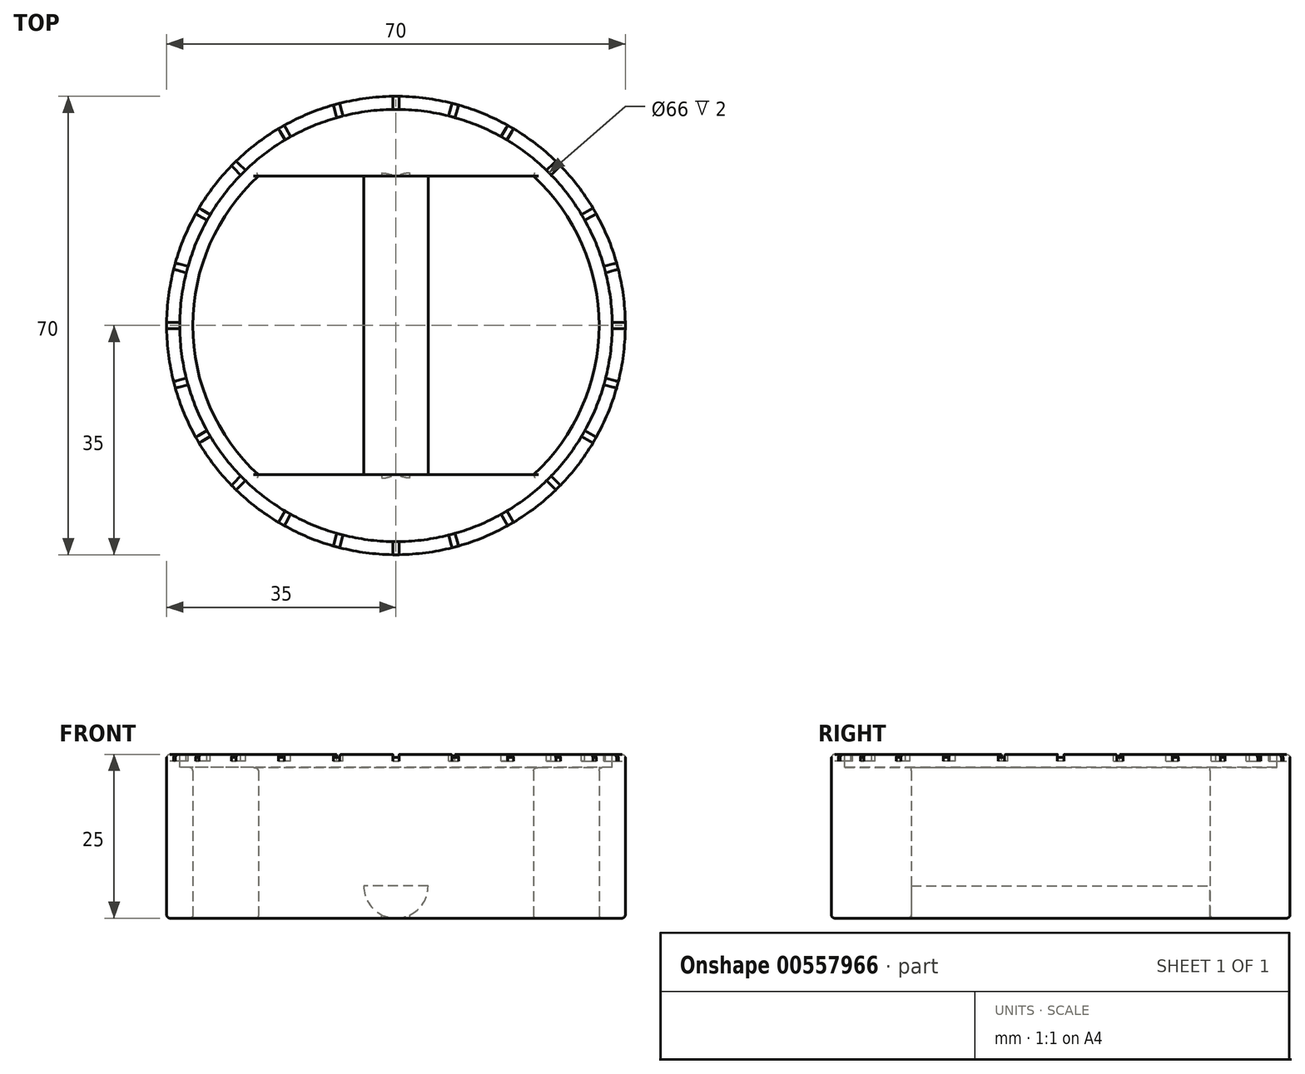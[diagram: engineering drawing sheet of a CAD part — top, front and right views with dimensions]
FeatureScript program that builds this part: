
annotation { "Feature Type Name" : "Feature", "Feature Type Description" : "" }
export const myFeature = defineFeature(function(context is Context, id is Id, definition is map)
    precondition{}
    {
        {
            var Q0;
            Q0=qCreatedBy(makeId("Top.planeOp"),FACE);
            var sketch = newSketch(context, id + "F0", { "sketchPlane" : qUnion([Q0])});
            skCircle(sketch, "E0", {"center": v(0, 0) * mm, "radius": 35 * mm});
            skLineSegment(sketch, "E1", {"start": v(-21, -22.8) * mm, "end": v(21, -22.8) * mm});
            skLineSegment(sketch, "E2", {"start": v(-21, 22.8) * mm, "end": v(21, 22.8) * mm});
            skArc(sketch, "E3", {"start": v(-21, 22.8) * mm, "mid": v(-31, 0) * mm, "end": v(-21, -22.8) * mm});
            skArc(sketch, "E4.trimOffspring", {"start": v(21, -22.8) * mm, "mid": v(31, 0) * mm, "end": v(21, 22.8) * mm});
            skSolve(sketch);
        }
        {
            var Q0;
            Q0 = qSketchRegion(id + "F0", true);
            extrude(context, id + "F1", {"entities" : qUnion([Q0]), "depth" : 25 * mm, "offsetDistance" : 25 * mm});
        }
        {
            var Q0;
            Q0=makeQuery(id+"F1.opExtrude","CAP_FACE",FACE,{"disambiguationData":[OSD([sQuery(id+"F0.wireOp",EDGE,"E0"),sQuery(id+"F0.wireOp",EDGE,"E1"),sQuery(id+"F0.wireOp",EDGE,"E2"),sQuery(id+"F0.wireOp",EDGE,"E3"),sQuery(id+"F0.wireOp",EDGE,"E4.trimOffspring")])],"isStart":false});
            var sketch = newSketch(context, id + "F2", { "sketchPlane" : qUnion([Q0])});
            skCircle(sketch, "E5.0", {"center": v(0, 0) * mm, "radius": 33 * mm});
            skSolve(sketch);
        }
        {
            var Q0;
            Q0 = qSketchRegion(id + "F2", true);
            extrude(context, id + "F3", {"entities" : qUnion([Q0]), "operationType" : NewBodyOperationType.REMOVE, "oppositeDirection" : true, "depth" : 2 * mm, "offsetDistance" : 25 * mm});
        }
        {
            var Q0;
            Q0=qCreatedBy(makeId("Front.planeOp"),FACE);
            var sketch = newSketch(context, id + "F4", { "sketchPlane" : qUnion([Q0])});
            skArc(sketch, "E6", {"start": v(-4.9, 4.9) * mm, "mid": v(0, 0) * mm, "end": v(4.9, 4.9) * mm});
            skLineSegment(sketch, "E7", {"start": v(-4.9, 4.9) * mm, "end": v(4.9, 4.9) * mm});
            skSolve(sketch);
        }
        {
            var Q0;
            Q0 = qSketchRegion(id + "F4", true);
            var Q1;
            Q1=makeQuery(id+"F1.opExtrude","SWEPT_FACE",FACE,{"disambiguationData":[OSD([sQuery(id+"F0.wireOp",EDGE,"E1")])]});
            var Q2;
            Q2=makeQuery(id+"F1.opExtrude","SWEPT_FACE",FACE,{"disambiguationData":[OSD([sQuery(id+"F0.wireOp",EDGE,"E2")])]});
            extrude(context, id + "F5", {"entities" : qUnion([Q0]), "operationType" : NewBodyOperationType.ADD, "endBound" : BoundingType.UP_TO_SURFACE, "depth" : 25 * mm, "endBoundEntityFace" : qUnion([Q1]), "offsetDistance" : 25 * mm, "hasSecondDirection" : true, "secondDirectionBound" : BoundingType.UP_TO_SURFACE, "secondDirectionOppositeDirection" : true, "secondDirectionDepth" : 25 * mm, "secondDirectionBoundEntityFace" : qUnion([Q2])});
        }
        {
            var Q0;
            Q0=makeQuery(id+"F3.boolean.opBoolean","COPY",EDGE,{"derivedFrom":makeQuery(id+"F3.opExtrude","CAP_EDGE",EDGE,{"disambiguationData":[OSD([sQuery(id+"F2.wireOp",EDGE,"E5.0")])],"isStart":true})});
            var Q1;
            Q1=makeQuery(id+"F1.opExtrude","CAP_EDGE",EDGE,{"disambiguationData":[OSD([sQuery(id+"F0.wireOp",EDGE,"E0")])],"isStart":false});
            var Q2;
            Q2=makeQuery(id+"F3.boolean.opBoolean","INTERSECT",EDGE,{"derivedFrom":[makeQuery(id+"F1.opExtrude","SWEPT_FACE",FACE,{"disambiguationData":[OSD([sQuery(id+"F0.wireOp",EDGE,"E3")])]}),makeQuery(id+"F3.opExtrude","CAP_FACE",FACE,{"disambiguationData":[OSD([sQuery(id+"F2.wireOp",EDGE,"E5.0")])],"isStart":false})]});
            var Q3;
            Q3=makeQuery(id+"F3.boolean.opBoolean","INTERSECT",EDGE,{"derivedFrom":[makeQuery(id+"F1.opExtrude","SWEPT_FACE",FACE,{"disambiguationData":[OSD([sQuery(id+"F0.wireOp",EDGE,"E4.trimOffspring")])]}),makeQuery(id+"F3.opExtrude","CAP_FACE",FACE,{"disambiguationData":[OSD([sQuery(id+"F2.wireOp",EDGE,"E5.0")])],"isStart":false})]});
            var Q4;
            Q4=makeQuery(id+"F5.opExtrude","TWEAK_EDGE",EDGE,{"disambiguationData":[OD(0.0)],"derivedFrom":[makeQuery(id+"F4.imprint","IMPRINT",EDGE,{"derivedFrom":sQuery(id+"F4.wireOp",EDGE,"E6")}),makeQuery(id+"F4.imprint","IMPRINT",EDGE,{"derivedFrom":sQuery(id+"F4.wireOp",EDGE,"E7")})]});
            var Q5;
            Q5=makeQuery(id+"F5.opExtrude","TWEAK_EDGE",EDGE,{"disambiguationData":[OD(1.0)],"derivedFrom":[makeQuery(id+"F4.imprint","IMPRINT",EDGE,{"derivedFrom":sQuery(id+"F4.wireOp",EDGE,"E6")}),makeQuery(id+"F4.imprint","IMPRINT",EDGE,{"derivedFrom":sQuery(id+"F4.wireOp",EDGE,"E7")})]});
            var Q6;
            {var subQ0=sQuery(id+"F0.wireOp",EDGE,"E4.trimOffspring");var subQ1=sQuery(id+"F0.wireOp",EDGE,"E2");Q6=makeQuery(id+"F5.boolean.opBoolean","SPLIT",EDGE,{"disambiguationData":[TD([makeQuery(id+"F1.opExtrude","SWEPT_FACE",FACE,{"disambiguationData":[OSD([subQ0])]})])],"derivedFrom":makeQuery(id+"F1.opExtrude","CAP_EDGE",EDGE,{"disambiguationData":[OSD([subQ1])],"isStart":true})});}
            var Q7;
            {var subQ0=sQuery(id+"F0.wireOp",EDGE,"E3");var subQ1=sQuery(id+"F0.wireOp",EDGE,"E1");Q7=makeQuery(id+"F5.boolean.opBoolean","SPLIT",EDGE,{"disambiguationData":[TD([makeQuery(id+"F1.opExtrude","SWEPT_FACE",FACE,{"disambiguationData":[OSD([subQ0])]})])],"derivedFrom":makeQuery(id+"F1.opExtrude","CAP_EDGE",EDGE,{"disambiguationData":[OSD([subQ1])],"isStart":true})});}
            var Q8;
            Q8=makeQuery(id+"F1.opExtrude","CAP_EDGE",EDGE,{"disambiguationData":[OSD([sQuery(id+"F0.wireOp",EDGE,"E0")])],"isStart":true});
            var Q9;
            Q9=makeQuery(id+"F1.opExtrude","CAP_EDGE",EDGE,{"disambiguationData":[OSD([sQuery(id+"F0.wireOp",EDGE,"E3")])],"isStart":true});
            var Q10;
            Q10=makeQuery(id+"F1.opExtrude","CAP_EDGE",EDGE,{"disambiguationData":[OSD([sQuery(id+"F0.wireOp",EDGE,"E4.trimOffspring")])],"isStart":true});
            fillet(context, id + "F6", {"entities" : qUnion([Q0, Q1, Q2, Q3, Q4, Q5, Q6, Q7, Q8, Q9, Q10]), "radius" : 0.5 * mm, "tangentPropagation" : true, "allowEdgeOverflow" : false});
        }
        {
            var Q0;
            Q0=makeQuery(id+"F1.opExtrude","CAP_FACE",FACE,{"disambiguationData":[OSD([sQuery(id+"F0.wireOp",EDGE,"E0"),sQuery(id+"F0.wireOp",EDGE,"E1"),sQuery(id+"F0.wireOp",EDGE,"E2"),sQuery(id+"F0.wireOp",EDGE,"E3"),sQuery(id+"F0.wireOp",EDGE,"E4.trimOffspring")])],"isStart":false});
            var sketch = newSketch(context, id + "F7", { "sketchPlane" : qUnion([Q0])});
            skLineSegment(sketch, "E8.bottom", {"start": v(0.5, 33) * mm, "end": v(-0.5, 33) * mm});
            skLineSegment(sketch, "E8.top", {"start": v(0.5, 35) * mm, "end": v(-0.5, 35) * mm});
            skLineSegment(sketch, "E8.left", {"start": v(0.5, 33) * mm, "end": v(0.5, 35) * mm});
            skLineSegment(sketch, "E8.right", {"start": v(-0.5, 33) * mm, "end": v(-0.5, 35) * mm});
            skPoint(sketch, "E8.middle", {"position": v(0, 34) * mm});
            skLineSegment(sketch, "E9.1.0", {"start": v(9.54, 33.67) * mm, "end": v(8.57, 33.93) * mm});
            skLineSegment(sketch, "E9.1.1", {"start": v(9.02, 31.74) * mm, "end": v(8.06, 32) * mm});
            skPoint(sketch, "E9.1.2", {"position": v(8.8, 32.84) * mm});
            skLineSegment(sketch, "E9.1.3", {"start": v(8.06, 32) * mm, "end": v(8.57, 33.93) * mm});
            skLineSegment(sketch, "E9.1.4", {"start": v(9.02, 31.74) * mm, "end": v(9.54, 33.67) * mm});
            skLineSegment(sketch, "E9.2.0", {"start": v(17.93, 30.06) * mm, "end": v(17.07, 30.56) * mm});
            skLineSegment(sketch, "E9.2.1", {"start": v(16.93, 28.33) * mm, "end": v(16.07, 28.83) * mm});
            skPoint(sketch, "E9.2.2", {"position": v(17, 29.44) * mm});
            skLineSegment(sketch, "E9.2.3", {"start": v(16.07, 28.83) * mm, "end": v(17.07, 30.56) * mm});
            skLineSegment(sketch, "E9.2.4", {"start": v(16.93, 28.33) * mm, "end": v(17.93, 30.06) * mm});
            skLineSegment(sketch, "E9.3.0", {"start": v(25.1, 24.4) * mm, "end": v(24.4, 25.1) * mm});
            skLineSegment(sketch, "E9.3.1", {"start": v(23.69, 22.98) * mm, "end": v(22.98, 23.69) * mm});
            skPoint(sketch, "E9.3.2", {"position": v(24.04, 24.04) * mm});
            skLineSegment(sketch, "E9.3.3", {"start": v(22.98, 23.69) * mm, "end": v(24.4, 25.1) * mm});
            skLineSegment(sketch, "E9.3.4", {"start": v(23.69, 22.98) * mm, "end": v(25.1, 24.4) * mm});
            skLineSegment(sketch, "E9.4.0", {"start": v(30.56, 17.07) * mm, "end": v(30.06, 17.93) * mm});
            skLineSegment(sketch, "E9.4.1", {"start": v(28.83, 16.07) * mm, "end": v(28.33, 16.93) * mm});
            skPoint(sketch, "E9.4.2", {"position": v(29.44, 17) * mm});
            skLineSegment(sketch, "E9.4.3", {"start": v(28.33, 16.93) * mm, "end": v(30.06, 17.93) * mm});
            skLineSegment(sketch, "E9.4.4", {"start": v(28.83, 16.07) * mm, "end": v(30.56, 17.07) * mm});
            skLineSegment(sketch, "E9.5.0", {"start": v(33.93, 8.57) * mm, "end": v(33.67, 9.54) * mm});
            skLineSegment(sketch, "E9.5.1", {"start": v(32, 8.06) * mm, "end": v(31.74, 9.02) * mm});
            skPoint(sketch, "E9.5.2", {"position": v(32.84, 8.8) * mm});
            skLineSegment(sketch, "E9.5.3", {"start": v(31.74, 9.02) * mm, "end": v(33.67, 9.54) * mm});
            skLineSegment(sketch, "E9.5.4", {"start": v(32, 8.06) * mm, "end": v(33.93, 8.57) * mm});
            skLineSegment(sketch, "E9.6.0", {"start": v(35, -0.5) * mm, "end": v(35, 0.5) * mm});
            skLineSegment(sketch, "E9.6.1", {"start": v(33, -0.5) * mm, "end": v(33, 0.5) * mm});
            skPoint(sketch, "E9.6.2", {"position": v(34, 0) * mm});
            skLineSegment(sketch, "E9.6.3", {"start": v(33, 0.5) * mm, "end": v(35, 0.5) * mm});
            skLineSegment(sketch, "E9.6.4", {"start": v(33, -0.5) * mm, "end": v(35, -0.5) * mm});
            skLineSegment(sketch, "E9.7.0", {"start": v(33.67, -9.54) * mm, "end": v(33.93, -8.57) * mm});
            skLineSegment(sketch, "E9.7.1", {"start": v(31.74, -9.02) * mm, "end": v(32, -8.06) * mm});
            skPoint(sketch, "E9.7.2", {"position": v(32.84, -8.8) * mm});
            skLineSegment(sketch, "E9.7.3", {"start": v(32, -8.06) * mm, "end": v(33.93, -8.57) * mm});
            skLineSegment(sketch, "E9.7.4", {"start": v(31.74, -9.02) * mm, "end": v(33.67, -9.54) * mm});
            skLineSegment(sketch, "E9.8.0", {"start": v(30.06, -17.93) * mm, "end": v(30.56, -17.07) * mm});
            skLineSegment(sketch, "E9.8.1", {"start": v(28.33, -16.93) * mm, "end": v(28.83, -16.07) * mm});
            skPoint(sketch, "E9.8.2", {"position": v(29.44, -17) * mm});
            skLineSegment(sketch, "E9.8.3", {"start": v(28.83, -16.07) * mm, "end": v(30.56, -17.07) * mm});
            skLineSegment(sketch, "E9.8.4", {"start": v(28.33, -16.93) * mm, "end": v(30.06, -17.93) * mm});
            skLineSegment(sketch, "E9.9.0", {"start": v(24.4, -25.1) * mm, "end": v(25.1, -24.4) * mm});
            skLineSegment(sketch, "E9.9.1", {"start": v(22.98, -23.69) * mm, "end": v(23.69, -22.98) * mm});
            skPoint(sketch, "E9.9.2", {"position": v(24.04, -24.04) * mm});
            skLineSegment(sketch, "E9.9.3", {"start": v(23.69, -22.98) * mm, "end": v(25.1, -24.4) * mm});
            skLineSegment(sketch, "E9.9.4", {"start": v(22.98, -23.69) * mm, "end": v(24.4, -25.1) * mm});
            skLineSegment(sketch, "E9.10.0", {"start": v(17.07, -30.56) * mm, "end": v(17.93, -30.06) * mm});
            skLineSegment(sketch, "E9.10.1", {"start": v(16.07, -28.83) * mm, "end": v(16.93, -28.33) * mm});
            skPoint(sketch, "E9.10.2", {"position": v(17, -29.44) * mm});
            skLineSegment(sketch, "E9.10.3", {"start": v(16.93, -28.33) * mm, "end": v(17.93, -30.06) * mm});
            skLineSegment(sketch, "E9.10.4", {"start": v(16.07, -28.83) * mm, "end": v(17.07, -30.56) * mm});
            skLineSegment(sketch, "E9.11.0", {"start": v(8.57, -33.93) * mm, "end": v(9.54, -33.67) * mm});
            skLineSegment(sketch, "E9.11.1", {"start": v(8.06, -32) * mm, "end": v(9.02, -31.74) * mm});
            skPoint(sketch, "E9.11.2", {"position": v(8.8, -32.84) * mm});
            skLineSegment(sketch, "E9.11.3", {"start": v(9.02, -31.74) * mm, "end": v(9.54, -33.67) * mm});
            skLineSegment(sketch, "E9.11.4", {"start": v(8.06, -32) * mm, "end": v(8.57, -33.93) * mm});
            skLineSegment(sketch, "E9.12.0", {"start": v(-0.5, -35) * mm, "end": v(0.5, -35) * mm});
            skLineSegment(sketch, "E9.12.1", {"start": v(-0.5, -33) * mm, "end": v(0.5, -33) * mm});
            skPoint(sketch, "E9.12.2", {"position": v(0, -34) * mm});
            skLineSegment(sketch, "E9.12.3", {"start": v(0.5, -33) * mm, "end": v(0.5, -35) * mm});
            skLineSegment(sketch, "E9.12.4", {"start": v(-0.5, -33) * mm, "end": v(-0.5, -35) * mm});
            skLineSegment(sketch, "E9.13.0", {"start": v(-9.54, -33.67) * mm, "end": v(-8.57, -33.93) * mm});
            skLineSegment(sketch, "E9.13.1", {"start": v(-9.02, -31.74) * mm, "end": v(-8.06, -32) * mm});
            skPoint(sketch, "E9.13.2", {"position": v(-8.8, -32.84) * mm});
            skLineSegment(sketch, "E9.13.3", {"start": v(-8.06, -32) * mm, "end": v(-8.57, -33.93) * mm});
            skLineSegment(sketch, "E9.13.4", {"start": v(-9.02, -31.74) * mm, "end": v(-9.54, -33.67) * mm});
            skLineSegment(sketch, "E9.14.0", {"start": v(-17.93, -30.06) * mm, "end": v(-17.07, -30.56) * mm});
            skLineSegment(sketch, "E9.14.1", {"start": v(-16.93, -28.33) * mm, "end": v(-16.07, -28.83) * mm});
            skPoint(sketch, "E9.14.2", {"position": v(-17, -29.44) * mm});
            skLineSegment(sketch, "E9.14.3", {"start": v(-16.07, -28.83) * mm, "end": v(-17.07, -30.56) * mm});
            skLineSegment(sketch, "E9.14.4", {"start": v(-16.93, -28.33) * mm, "end": v(-17.93, -30.06) * mm});
            skLineSegment(sketch, "E9.15.0", {"start": v(-25.1, -24.4) * mm, "end": v(-24.4, -25.1) * mm});
            skLineSegment(sketch, "E9.15.1", {"start": v(-23.69, -22.98) * mm, "end": v(-22.98, -23.69) * mm});
            skPoint(sketch, "E9.15.2", {"position": v(-24.04, -24.04) * mm});
            skLineSegment(sketch, "E9.15.3", {"start": v(-22.98, -23.69) * mm, "end": v(-24.4, -25.1) * mm});
            skLineSegment(sketch, "E9.15.4", {"start": v(-23.69, -22.98) * mm, "end": v(-25.1, -24.4) * mm});
            skLineSegment(sketch, "E9.16.0", {"start": v(-30.56, -17.07) * mm, "end": v(-30.06, -17.93) * mm});
            skLineSegment(sketch, "E9.16.1", {"start": v(-28.83, -16.07) * mm, "end": v(-28.33, -16.93) * mm});
            skPoint(sketch, "E9.16.2", {"position": v(-29.44, -17) * mm});
            skLineSegment(sketch, "E9.16.3", {"start": v(-28.33, -16.93) * mm, "end": v(-30.06, -17.93) * mm});
            skLineSegment(sketch, "E9.16.4", {"start": v(-28.83, -16.07) * mm, "end": v(-30.56, -17.07) * mm});
            skPoint(sketch, "E9.center", {"position": v(0, 0) * mm});
            skLineSegment(sketch, "E9.anchor1", {"start": v(0, 0) * mm, "end": v(-0.5, 33) * mm, "construction": true});
            skLineSegment(sketch, "E9.anchor2", {"start": v(0, 0) * mm, "end": v(-0.5, 33) * mm, "construction": true});
            skLineSegment(sketch, "E10.3.17.0", {"start": v(-32, -8.06) * mm, "end": v(-31.74, -9.02) * mm});
            skLineSegment(sketch, "E10.5.17.0", {"start": v(-33.93, -8.57) * mm, "end": v(-33.67, -9.54) * mm});
            skPoint(sketch, "E10.6.17.0", {"position": v(-32.84, -8.8) * mm});
            skLineSegment(sketch, "E10.7.17.0", {"start": v(-31.74, -9.02) * mm, "end": v(-33.67, -9.54) * mm});
            skLineSegment(sketch, "E10.10.17.0", {"start": v(-32, -8.06) * mm, "end": v(-33.93, -8.57) * mm});
            skLineSegment(sketch, "E10.3.18.0", {"start": v(-33, 0.5) * mm, "end": v(-33, -0.5) * mm});
            skLineSegment(sketch, "E10.5.18.0", {"start": v(-35, 0.5) * mm, "end": v(-35, -0.5) * mm});
            skPoint(sketch, "E10.6.18.0", {"position": v(-34, 0) * mm});
            skLineSegment(sketch, "E10.7.18.0", {"start": v(-33, -0.5) * mm, "end": v(-35, -0.5) * mm});
            skLineSegment(sketch, "E10.10.18.0", {"start": v(-33, 0.5) * mm, "end": v(-35, 0.5) * mm});
            skLineSegment(sketch, "E10.3.19.0", {"start": v(-31.74, 9.02) * mm, "end": v(-32, 8.06) * mm});
            skLineSegment(sketch, "E10.5.19.0", {"start": v(-33.67, 9.54) * mm, "end": v(-33.93, 8.57) * mm});
            skPoint(sketch, "E10.6.19.0", {"position": v(-32.84, 8.8) * mm});
            skLineSegment(sketch, "E10.7.19.0", {"start": v(-32, 8.06) * mm, "end": v(-33.93, 8.57) * mm});
            skLineSegment(sketch, "E10.10.19.0", {"start": v(-31.74, 9.02) * mm, "end": v(-33.67, 9.54) * mm});
            skLineSegment(sketch, "E10.3.20.0", {"start": v(-28.33, 16.93) * mm, "end": v(-28.83, 16.07) * mm});
            skLineSegment(sketch, "E10.5.20.0", {"start": v(-30.06, 17.93) * mm, "end": v(-30.56, 17.07) * mm});
            skPoint(sketch, "E10.6.20.0", {"position": v(-29.44, 17) * mm});
            skLineSegment(sketch, "E10.7.20.0", {"start": v(-28.83, 16.07) * mm, "end": v(-30.56, 17.07) * mm});
            skLineSegment(sketch, "E10.10.20.0", {"start": v(-28.33, 16.93) * mm, "end": v(-30.06, 17.93) * mm});
            skLineSegment(sketch, "E10.3.21.0", {"start": v(-22.98, 23.69) * mm, "end": v(-23.69, 22.98) * mm});
            skLineSegment(sketch, "E10.5.21.0", {"start": v(-24.4, 25.1) * mm, "end": v(-25.1, 24.4) * mm});
            skPoint(sketch, "E10.6.21.0", {"position": v(-24.04, 24.04) * mm});
            skLineSegment(sketch, "E10.7.21.0", {"start": v(-23.69, 22.98) * mm, "end": v(-25.1, 24.4) * mm});
            skLineSegment(sketch, "E10.10.21.0", {"start": v(-22.98, 23.69) * mm, "end": v(-24.4, 25.1) * mm});
            skLineSegment(sketch, "E10.3.22.0", {"start": v(-16.07, 28.83) * mm, "end": v(-16.93, 28.33) * mm});
            skLineSegment(sketch, "E10.5.22.0", {"start": v(-17.07, 30.56) * mm, "end": v(-17.93, 30.06) * mm});
            skPoint(sketch, "E10.6.22.0", {"position": v(-17, 29.44) * mm});
            skLineSegment(sketch, "E10.7.22.0", {"start": v(-16.93, 28.33) * mm, "end": v(-17.93, 30.06) * mm});
            skLineSegment(sketch, "E10.10.22.0", {"start": v(-16.07, 28.83) * mm, "end": v(-17.07, 30.56) * mm});
            skLineSegment(sketch, "E11.3.23.0", {"start": v(-8.06, 32) * mm, "end": v(-9.02, 31.74) * mm});
            skLineSegment(sketch, "E11.5.23.0", {"start": v(-8.57, 33.93) * mm, "end": v(-9.54, 33.67) * mm});
            skPoint(sketch, "E11.6.23.0", {"position": v(-8.8, 32.84) * mm});
            skLineSegment(sketch, "E11.7.23.0", {"start": v(-9.02, 31.74) * mm, "end": v(-9.54, 33.67) * mm});
            skLineSegment(sketch, "E11.10.23.0", {"start": v(-8.06, 32) * mm, "end": v(-8.57, 33.93) * mm});
            skSolve(sketch);
        }
        {
            var Q0;
            Q0 = qSketchRegion(id + "F7", true);
            extrude(context, id + "F8", {"entities" : qUnion([Q0]), "operationType" : NewBodyOperationType.REMOVE, "oppositeDirection" : true, "depth" : 1 * mm, "offsetDistance" : 25 * mm});
        }
    });
